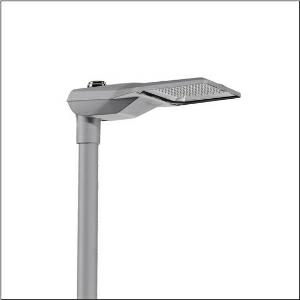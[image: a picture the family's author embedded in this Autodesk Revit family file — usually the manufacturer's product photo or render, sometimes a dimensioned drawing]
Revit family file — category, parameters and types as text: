
# Revit family: streetlight_sl_21_midi___st0_5a_5xe7b47n08mb_0aeb
name_source: partatom
category: Lighting Fixtures
units: mm (PartAtom-declared; Revit-internal decimal feet)

## family parameters
Cut with Voids When Loaded = No
Host = Face
Light Source = No
Part Type = Normal
Room Calculation Point = No
Round Connector Dimension = Use Diameter
Shared = No

## types (1)
- --- (1 x LED, 20180 lm, 147 W, 4000K)
    Apparent Load = 147 VA
    CIE Flux Codes = 41 75 97 100 100
    Color Rendering = 70
    Color Temperature = 4000K
    Default Elevation = 1800 mm
    Description = Streetlight SL 21 midi, mast luminaire, primary light control with lens, of PMMA, primary optical cover: cover, of toughened safety glass, transparent, light distribution: ST0.5a, light emission: direct distribution, primary light characteristic: asymmetric, installation type: side-entry, LED, 3G 2.5mm², High Power LED, rated luminous flux: 20.180lm, luminous efficacy: 137lm/W, light colour: 740, colour temperature: 4000K, control gear: NEMA (7pin), control: overheat protection, pre-setting: linear dimming characteristic, constant luminous flux control, time-dependent luminous flux control, flexible luminous flux parameterisation, mains connection: 220..240V, AC, 50/60Hz, connection cable pre-assembled, cable length: 12,5m, wiring characteristics: H05VV-F, start of lifetime: 147W, end of service life: 155W, reduction: 65W, luminaire housing, of diecast aluminium (EN AC-44300), powder-coated, Siteco® metallic grey (DB 702S), corrosivity category C5 mid according to DIN EN ISO 12944, multi-level sealing system, sealing non-destructively replaceable, inclination adjustable: 0°, 5°, 10°, 15°, length: 644mm, width: 335mm, height: 110mm, spigot size: 42mm (side-entry), mounting height: 4..8m, protection rating (complete): IP66, insulation class (complete): insulation class I (protective earthing), certification: CE, ENEC, ENEC+, VDE, impact resistance: IK10, permissible operating ambient temperature for outdoor applications: -40..+50°C, standard-compliant lighting for roads and squares, packaging unit: 1 piece

Light Distribution: ST0.5a
    Height = 111 mm
    Lamp = 1 x LED
    Lamp Light Flux = 20180 lm
    Lamp Power = 147 W
    Lamp count = 1
    Length = 644 mm
    Luminous efficacy = 137 lm/W
    Manufacturer = Siteco
    ModVariant = No
    Model = 5XE7B47N08MB
    Number of Poles = 1
    OnlyDefault = Yes
    Power Factor = 1
    Product Name = Streetlight SL 21 midi | ST0.5a
    Product group = mast luminaire | pylon top
    ProductGroupID = 6100
    Protection Class = Protection class I
    Protection Degree = IP 66
    RLX_Detail_Level = 1
    RLX_Emergency_Light_Flux = 0 lm
    RLX_Emergency_Type = 0
    RLX_Emergency_Type_DB = No
    RlxData = <blob elided: 37493 chars, md5=bc86b70c>
    Socket = socket
    Standby Power = 0 W
    System Light Flux = 20180 lm
    System Power = 147 W
    Type Comments = factory setting: luminous flux: 100 % | dim-lin: 254 | 750 mA
    Type Image = l_1294377.jpg
    URL = http://relux.com
    VarID = @adj_158741
    Voltage = 0 V
    Weight = 0.00 kg
    Width = 336 mm

## geometry (parser evidence)
native form markers: Blend x4, Sweep x12
no freeform markers — native parametric forms only
